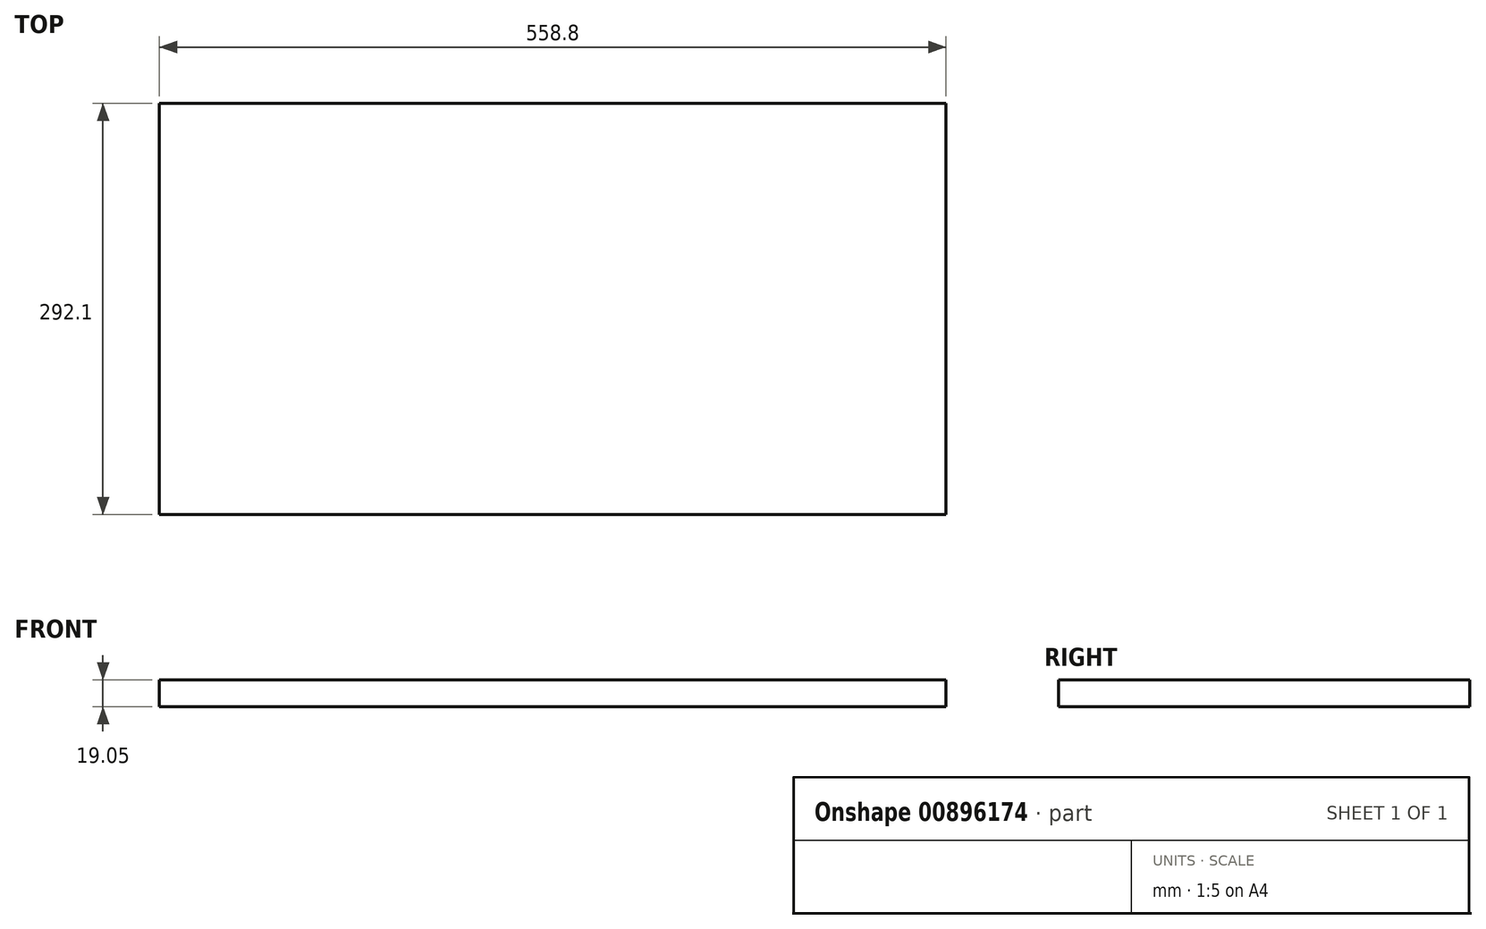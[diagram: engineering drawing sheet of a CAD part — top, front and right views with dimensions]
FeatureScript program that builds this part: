
annotation { "Feature Type Name" : "Feature", "Feature Type Description" : "" }
export const myFeature = defineFeature(function(context is Context, id is Id, definition is map)
    precondition{}
    {
        {
            var Q0;
            Q0=qCreatedBy(makeId("Top.planeOp"),FACE);
            var sketch = newSketch(context, id + "F0", { "sketchPlane" : qUnion([Q0])});
            skLineSegment(sketch, "E0.bottom", {"start": v(0, 0) * mm, "end": v(558.8, 0) * mm});
            skLineSegment(sketch, "E0.top", {"start": v(0, -292.1) * mm, "end": v(558.8, -292.1) * mm});
            skLineSegment(sketch, "E0.left", {"start": v(0, 0) * mm, "end": v(0, -292.1) * mm});
            skLineSegment(sketch, "E0.right", {"start": v(558.8, 0) * mm, "end": v(558.8, -292.1) * mm});
            skSolve(sketch);
        }
        {
            var Q0;
            Q0=makeQuery(id+"F0.imprint","IMPRINT",FACE,{"disambiguationData":[TD([[makeQuery(id+"F0.imprint","IMPRINT",EDGE,{"derivedFrom":sQuery(id+"F0.wireOp",EDGE,"E0.bottom")}),-1.0]])]});
            extrude(context, id + "F1", {"entities" : qUnion([Q0]), "depth" : 19.05 * mm, "offsetDistance" : 25.4 * mm});
        }
    });
